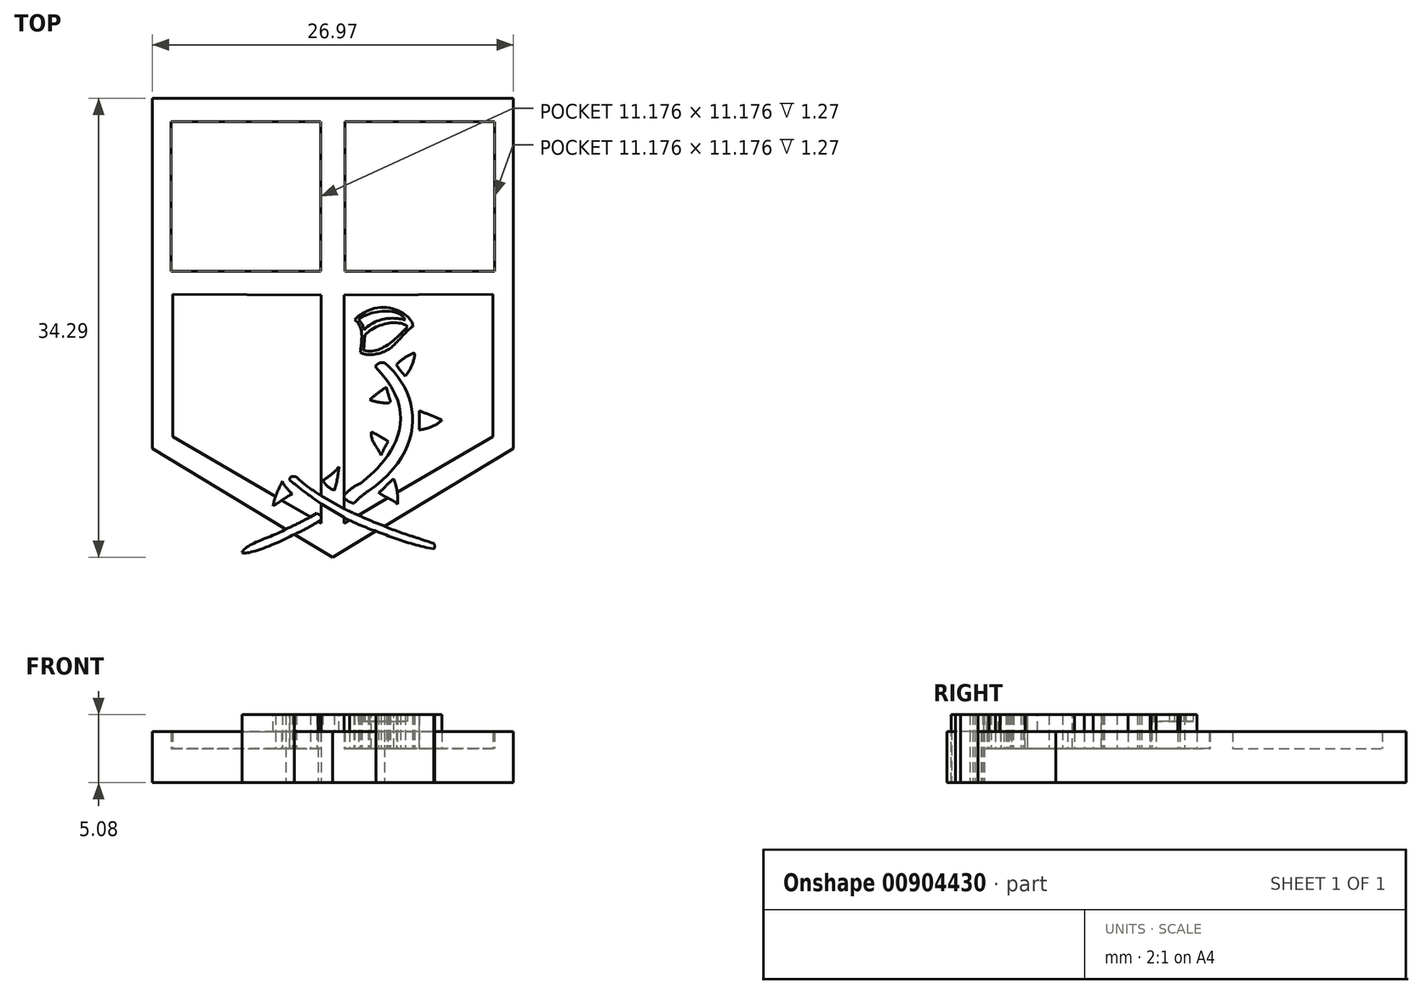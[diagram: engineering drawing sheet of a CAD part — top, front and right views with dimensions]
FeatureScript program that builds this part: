
annotation { "Feature Type Name" : "Feature", "Feature Type Description" : "" }
export const myFeature = defineFeature(function(context is Context, id is Id, definition is map)
    precondition{}
    {
        {
            var Q0;
            Q0=qCreatedBy(makeId("Top.planeOp"),FACE);
            var sketch = newSketch(context, id + "F0", { "sketchPlane" : qUnion([Q0])});
            skLineSegment(sketch, "E0", {"start": v(-8.88, 24.55) * mm, "end": v(18.1, 24.55) * mm});
            skLineSegment(sketch, "E1", {"start": v(18.1, 24.55) * mm, "end": v(18.1, -1.61) * mm});
            skLineSegment(sketch, "E2", {"start": v(-8.88, 24.55) * mm, "end": v(-8.88, -1.61) * mm});
            skPoint(sketch, "E3.endSnap0", {"position": v(4.6, -10.54) * mm});
            skLineSegment(sketch, "E4", {"start": v(-8.88, -1.61) * mm, "end": v(4.6, -9.74) * mm});
            skLineSegment(sketch, "E5", {"start": v(18.1, -1.61) * mm, "end": v(4.6, -9.74) * mm});
            skPoint(sketch, "E6", {"position": v(4.6, -9.27) * mm});
            skFitSpline(sketch, "E7", {"points": [v(1.75, -8.02) * mm, v(-2.16, -9.4) * mm], "startDerivative": vector(-3.65, -1.95) * mm, "endDerivative": vector(-1.46, 0.61) * mm});
            skFitSpline(sketch, "E8", {"points": [v(-2.16, -9.4) * mm, v(1.1, -7.64) * mm], "startDerivative": vector(0.54, 2) * mm, "endDerivative": vector(3.2, 1.91) * mm});
            skFitSpline(sketch, "E9", {"points": [v(12.16, -9.11) * mm, v(12.16, -8.7) * mm], "startDerivative": vector(0.36, 0.66) * mm, "endDerivative": vector(-0.03, 0.11) * mm});
            skLineSegment(sketch, "E10", {"start": v(-7.35, 9.92) * mm, "end": v(-7.35, -0.73) * mm});
            skLineSegment(sketch, "E11", {"start": v(-7.35, -0.73) * mm, "end": v(3.75, -7.2) * mm});
            skLineSegment(sketch, "E12", {"start": v(3.75, -7.2) * mm, "end": v(3.75, 9.86) * mm});
            skLineSegment(sketch, "E13", {"start": v(3.75, 9.86) * mm, "end": v(-7.35, 9.92) * mm});
            skLineSegment(sketch, "E14.MirrorCS", {"start": v(5.46, -7.2) * mm, "end": v(5.46, 9.86) * mm});
            skLineSegment(sketch, "E15.MirrorCS", {"start": v(5.46, 9.86) * mm, "end": v(16.56, 9.92) * mm});
            skLineSegment(sketch, "E16.MirrorCS", {"start": v(16.56, 9.92) * mm, "end": v(16.56, -0.73) * mm});
            skLineSegment(sketch, "E17.MirrorCS", {"start": v(16.56, -0.73) * mm, "end": v(5.46, -7.2) * mm});
            skLineSegment(sketch, "E18", {"start": v(-7.48, 11.6) * mm, "end": v(3.7, 11.6) * mm});
            skLineSegment(sketch, "E19", {"start": v(3.7, 11.6) * mm, "end": v(3.7, 22.79) * mm});
            skLineSegment(sketch, "E20", {"start": v(3.7, 22.79) * mm, "end": v(-7.48, 22.79) * mm});
            skLineSegment(sketch, "E21", {"start": v(-7.48, 22.79) * mm, "end": v(-7.48, 11.6) * mm});
            skLineSegment(sketch, "E22.MirrorCS", {"start": v(5.51, 11.6) * mm, "end": v(5.51, 22.79) * mm});
            skLineSegment(sketch, "E23.MirrorCS", {"start": v(5.51, 22.79) * mm, "end": v(16.69, 22.79) * mm});
            skLineSegment(sketch, "E24.MirrorCS", {"start": v(16.69, 11.6) * mm, "end": v(5.51, 11.6) * mm});
            skLineSegment(sketch, "E25.MirrorCS", {"start": v(16.69, 22.79) * mm, "end": v(16.69, 11.6) * mm});
            skFitSpline(sketch, "E26", {"points": [v(7.84, -7.79) * mm, v(12.16, -9.11) * mm], "startDerivative": vector(4.26, -1.68) * mm, "endDerivative": vector(4.49, -0.76) * mm});
            skFitSpline(sketch, "E27", {"points": [v(8.47, -7.41) * mm, v(12.16, -8.7) * mm], "startDerivative": vector(3.35, -1.51) * mm, "endDerivative": vector(3.74, -1.29) * mm});
            skFitSpline(sketch, "E28", {"points": [v(8.47, -7.41) * mm, v(6.52, -6.59) * mm], "startDerivative": vector(-2.19, 0.84) * mm, "endDerivative": vector(-1.81, 0.92) * mm});
            skFitSpline(sketch, "E29", {"points": [v(5.86, -6.98) * mm, v(7.84, -7.79) * mm], "startDerivative": vector(1.98, -1) * mm, "endDerivative": vector(2.05, -0.7) * mm});
            skFitSpline(sketch, "E30", {"points": [v(5.86, -6.98) * mm, v(5.46, -6.77) * mm], "startDerivative": vector(-0.5, 0.16) * mm, "endDerivative": vector(-0.31, 0.24) * mm});
            skLineSegment(sketch, "E31", {"start": v(5.46, -6.77) * mm, "end": v(3.75, -5.74) * mm});
            skFitSpline(sketch, "E32", {"points": [v(1.4, -3.97) * mm, v(1.89, -3.75) * mm], "startDerivative": vector(-0.2, 1.1) * mm, "endDerivative": vector(0.2, -0.15) * mm});
            skFitSpline(sketch, "E33", {"points": [v(3.75, -5.74) * mm, v(1.4, -3.97) * mm], "startDerivative": vector(-2.5, 1.72) * mm, "endDerivative": vector(-2.23, 1.88) * mm});
            skFitSpline(sketch, "E34", {"points": [v(1.89, -3.75) * mm, v(3.75, -5.14) * mm], "startDerivative": vector(1.45, -1.45) * mm, "endDerivative": vector(2.03, -1.25) * mm});
            skLineSegment(sketch, "E35", {"start": v(3.75, -5.14) * mm, "end": v(5.46, -6.11) * mm});
            skFitSpline(sketch, "E36", {"points": [v(5.46, -6.11) * mm, v(6.52, -6.59) * mm], "startDerivative": vector(0.85, -0.41) * mm, "endDerivative": vector(1.1, -0.4) * mm});
            skFitSpline(sketch, "E37", {"points": [v(1.75, -8.02) * mm, v(3.52, -7.07) * mm], "startDerivative": vector(1.94, 0.84) * mm, "endDerivative": vector(1.5, 1.02) * mm});
            skFitSpline(sketch, "E38", {"points": [v(2.94, -6.74) * mm, v(1.1, -7.64) * mm], "startDerivative": vector(-1.7, -0.83) * mm, "endDerivative": vector(-1.92, -0.81) * mm});
            skLineSegment(sketch, "E39", {"start": v(2.94, -6.74) * mm, "end": v(3.42, -6.45) * mm});
            skLineSegment(sketch, "E40", {"start": v(3.42, -6.45) * mm, "end": v(3.95, -6.8) * mm});
            skLineSegment(sketch, "E41", {"start": v(3.95, -6.8) * mm, "end": v(3.52, -7.07) * mm});
            skFitSpline(sketch, "E42", {"points": [v(8.03, -4.9) * mm, v(9.45, -5.78) * mm], "startDerivative": vector(1.28, -1) * mm, "endDerivative": vector(1.12, -1.08) * mm});
            skFitSpline(sketch, "E43", {"points": [v(9.45, -5.78) * mm, v(9.15, -3.88) * mm], "startDerivative": vector(0.12, 1.99) * mm, "endDerivative": vector(-0.76, 1.93) * mm});
            skFitSpline(sketch, "E44", {"points": [v(9.15, -3.88) * mm, v(8.03, -4.9) * mm], "startDerivative": vector(-1.28, -0.9) * mm, "endDerivative": vector(-0.9, -0.5) * mm});
            skFitSpline(sketch, "E45", {"points": [v(3.87, -4) * mm, v(5.07, -2.97) * mm], "startDerivative": vector(1.37, 0.85) * mm, "endDerivative": vector(1.04, 1.3) * mm});
            skFitSpline(sketch, "E46", {"points": [v(5.07, -2.97) * mm, v(4.73, -4.75) * mm], "startDerivative": vector(-0.15, -1.83) * mm, "endDerivative": vector(-0.54, -1.7) * mm});
            skFitSpline(sketch, "E47", {"points": [v(4.73, -4.75) * mm, v(3.87, -4) * mm], "startDerivative": vector(-1.15, 0.48) * mm, "endDerivative": vector(-0.35, 0.92) * mm});
            skFitSpline(sketch, "E48", {"points": [v(0.16, -5.9) * mm, v(0.85, -4.05) * mm], "startDerivative": vector(0.2, 1.87) * mm, "endDerivative": vector(0.89, 1.88) * mm});
            skFitSpline(sketch, "E49", {"points": [v(1.57, -5.02) * mm, v(0.85, -4.05) * mm], "startDerivative": vector(-0.88, 0.94) * mm, "endDerivative": vector(-0.18, 0.91) * mm});
            skFitSpline(sketch, "E50", {"points": [v(1.57, -5.02) * mm, v(0.16, -5.9) * mm], "startDerivative": vector(-1.49, -0.74) * mm, "endDerivative": vector(-1.1, -0.6) * mm});
            skFitSpline(sketch, "E51", {"points": [v(7.78, 4.5) * mm, v(6.68, -4.2) * mm], "startDerivative": vector(11.95, -11.98) * mm, "endDerivative": vector(-5.34, -3.98) * mm});
            skFitSpline(sketch, "E52", {"points": [v(7.25, -4.8) * mm, v(8.45, 4.81) * mm], "startDerivative": vector(12.9, 8.87) * mm, "endDerivative": vector(-8.74, 7.47) * mm});
            skFitSpline(sketch, "E53", {"points": [v(8.45, 4.81) * mm, v(7.78, 4.5) * mm], "startDerivative": vector(-0.97, 0.03) * mm, "endDerivative": vector(-0.4, -0.7) * mm});
            skFitSpline(sketch, "E54", {"points": [v(6.19, -5.71) * mm, v(5.34, -5.22) * mm], "startDerivative": vector(-0.98, 0.12) * mm, "endDerivative": vector(-0.63, 0.58) * mm});
            skFitSpline(sketch, "E55", {"points": [v(6.68, -4.2) * mm, v(5.34, -5.22) * mm], "startDerivative": vector(-1.96, -0.9) * mm, "endDerivative": vector(-1.14, -1.14) * mm});
            skFitSpline(sketch, "E56", {"points": [v(7.25, -4.8) * mm, v(6.19, -5.71) * mm], "startDerivative": vector(-1.17, -0.88) * mm, "endDerivative": vector(-1, -1.1) * mm});
            skFitSpline(sketch, "E57", {"points": [v(11.09, 1.2) * mm, v(12.76, 0.5) * mm], "startDerivative": vector(1.54, -0.64) * mm, "endDerivative": vector(1.6, -0.83) * mm});
            skFitSpline(sketch, "E58", {"points": [v(12.76, 0.5) * mm, v(11.06, -0.22) * mm], "startDerivative": vector(-1.18, -1.1) * mm, "endDerivative": vector(-2.39, -0.32) * mm});
            skFitSpline(sketch, "E59", {"points": [v(11.06, -0.22) * mm, v(11.09, 1.2) * mm], "startDerivative": vector(0.15, 1.56) * mm, "endDerivative": vector(0.02, 1.29) * mm});
            skFitSpline(sketch, "E60", {"points": [v(8.61, 2.97) * mm, v(8.92, 1.9) * mm], "startDerivative": vector(0.27, -1.1) * mm, "endDerivative": vector(0.42, -1.11) * mm});
            skFitSpline(sketch, "E61", {"points": [v(8.92, 1.9) * mm, v(8.8, 1.78) * mm], "startDerivative": vector(-0.17, -0.04) * mm, "endDerivative": vector(-0.09, -0.2) * mm});
            skFitSpline(sketch, "E62", {"points": [v(8.8, 1.78) * mm, v(7.36, 2.02) * mm], "startDerivative": vector(-1.48, -0.03) * mm, "endDerivative": vector(-1.23, 0.43) * mm});
            skFitSpline(sketch, "E63", {"points": [v(7.36, 2.02) * mm, v(8.61, 2.97) * mm], "startDerivative": vector(1.2, 1.04) * mm, "endDerivative": vector(1.34, 0.77) * mm});
            skFitSpline(sketch, "E64", {"points": [v(9.37, 4.66) * mm, v(10.02, 3.79) * mm], "startDerivative": vector(0.47, -0.95) * mm, "endDerivative": vector(0.76, -0.8) * mm});
            skFitSpline(sketch, "E65", {"points": [v(10.02, 3.79) * mm, v(10.73, 5.44) * mm], "startDerivative": vector(1.13, 1.35) * mm, "endDerivative": vector(0.16, 1.94) * mm});
            skFitSpline(sketch, "E66", {"points": [v(10.73, 5.44) * mm, v(10.65, 5.52) * mm], "startDerivative": vector(-0.05, 0.12) * mm, "endDerivative": vector(-0.1, 0) * mm});
            skFitSpline(sketch, "E67", {"points": [v(10.65, 5.52) * mm, v(9.37, 4.66) * mm], "startDerivative": vector(-1.45, -0.6) * mm, "endDerivative": vector(-1.01, -1.07) * mm});
            skFitSpline(sketch, "E68", {"points": [v(7.5, -0.37) * mm, v(8.76, -1.1) * mm], "startDerivative": vector(1.25, -0.62) * mm, "endDerivative": vector(1.27, -0.81) * mm});
            skFitSpline(sketch, "E69", {"points": [v(8.76, -1.1) * mm, v(8.22, -2.12) * mm], "startDerivative": vector(-0.7, -0.88) * mm, "endDerivative": vector(-0.4, -1.1) * mm});
            skFitSpline(sketch, "E70", {"points": [v(8.22, -2.12) * mm, v(7.5, -0.37) * mm], "startDerivative": vector(-0.73, 1.75) * mm, "endDerivative": vector(0.36, 2.07) * mm});
            skFitSpline(sketch, "E71", {"points": [v(6.53, 7.97) * mm, v(10.03, 8) * mm], "startDerivative": vector(1.06, 1.69) * mm, "endDerivative": vector(1.74, -3.54) * mm});
            skFitSpline(sketch, "E72", {"points": [v(10.03, 8) * mm, v(6.95, 7.24) * mm], "startDerivative": vector(-2.3, 0.65) * mm, "endDerivative": vector(-2.9, -3.02) * mm});
            skFitSpline(sketch, "E73", {"points": [v(6.92, 5.73) * mm, v(10.19, 7.48) * mm], "startDerivative": vector(3.52, -1.1) * mm, "endDerivative": vector(2.85, 3.03) * mm});
            skFitSpline(sketch, "E74", {"points": [v(10.19, 7.48) * mm, v(7.02, 6.87) * mm], "startDerivative": vector(-1.75, 1.7) * mm, "endDerivative": vector(-2.5, -2.76) * mm});
            skFitSpline(sketch, "E75", {"points": [v(6.53, 7.97) * mm, v(6.95, 7.24) * mm], "startDerivative": vector(0.64, -0.49) * mm, "endDerivative": vector(0.13, -1) * mm});
            skFitSpline(sketch, "E76", {"points": [v(7.02, 6.87) * mm, v(6.92, 5.73) * mm], "startDerivative": vector(-0.1, -1.14) * mm, "endDerivative": vector(-0.1, -1.14) * mm});
            skFitSpline(sketch, "E77", {"points": [v(6.24, 8) * mm, v(6.66, 5.57) * mm], "startDerivative": vector(2.32, -1.68) * mm, "endDerivative": vector(-0.2, -2.32) * mm});
            skFitSpline(sketch, "E78", {"points": [v(6.66, 5.57) * mm, v(8.91, 5.87) * mm], "startDerivative": vector(0.96, -0.74) * mm, "endDerivative": vector(2.53, 1.73) * mm});
            skFitSpline(sketch, "E79", {"points": [v(8.91, 5.87) * mm, v(10.59, 7.5) * mm], "startDerivative": vector(1.91, 1.72) * mm, "endDerivative": vector(1.75, 1.27) * mm});
            skFitSpline(sketch, "E80", {"points": [v(10.59, 7.5) * mm, v(10.57, 7.67) * mm], "startDerivative": vector(-0.02, 0.16) * mm, "endDerivative": vector(-0.02, 0.16) * mm});
            skFitSpline(sketch, "E81", {"points": [v(10.57, 7.67) * mm, v(6.24, 8) * mm], "startDerivative": vector(-0.95, 2.95) * mm, "endDerivative": vector(-5.37, -5.32) * mm});
            skSolve(sketch);
        }
        {
            var Q0;
            {var subQ5=sQuery(id+"F0.wireOp",EDGE,"E29");Q0=makeQuery(id+"F0.imprint","IMPRINT",FACE,{"disambiguationData":[TD([[makeQuery(id+"F0.imprint","IMPRINT",EDGE,{"derivedFrom":subQ5}),-1.0]])]});}
            var Q1;
            {var subQ0=sQuery(id+"F0.wireOp",EDGE,"E41");var subQ1=sQuery(id+"F0.wireOp",EDGE,"E12");var subQ2=makeQuery(id+"F0.imprint","INTERSECT",VERTEX,{"derivedFrom":[subQ1,subQ0]});Q1=makeQuery(id+"F0.imprint","IMPRINT",FACE,{"disambiguationData":[TD([[makeQuery(id+"F0.imprint","IMPRINT",EDGE,{"disambiguationData":[TD([[subQ2,-1.0]])],"derivedFrom":subQ1}),-1.0]])]});}
            var Q2;
            Q2=makeQuery(id+"F0.imprint","IMPRINT",FACE,{"disambiguationData":[TD([[makeQuery(id+"F0.imprint","IMPRINT",EDGE,{"derivedFrom":sQuery(id+"F0.wireOp",EDGE,"E0")}),-1.0]])]});
            var Q3;
            {var subQ0=sQuery(id+"F0.wireOp",EDGE,"E54");var subQ1=sQuery(id+"F0.wireOp",EDGE,"E14.MirrorCS");var subQ2=makeQuery(id+"F0.imprint","INTERSECT",VERTEX,{"derivedFrom":[subQ1,subQ0]});Q3=makeQuery(id+"F0.imprint","IMPRINT",FACE,{"disambiguationData":[TD([[makeQuery(id+"F0.imprint","IMPRINT",EDGE,{"disambiguationData":[TD([[subQ2,-1.0]])],"derivedFrom":subQ1}),1.0]])]});}
            extrude(context, id + "F1", {"entities" : qUnion([Q0, Q1, Q2, Q3]), "depth" : 3.8 * mm, "offsetDistance" : 25.4 * mm});
        }
        {
            var Q0;
            Q0=makeQuery(id+"F0.imprint","IMPRINT",FACE,{"disambiguationData":[TD([[makeQuery(id+"F0.imprint","IMPRINT",EDGE,{"derivedFrom":sQuery(id+"F0.wireOp",EDGE,"E18")}),1.0]])]});
            var Q1;
            Q1=makeQuery(id+"F0.imprint","IMPRINT",FACE,{"disambiguationData":[TD([[makeQuery(id+"F0.imprint","IMPRINT",EDGE,{"derivedFrom":sQuery(id+"F0.wireOp",EDGE,"E22.MirrorCS")}),-1.0]])]});
            var Q2;
            Q2=makeQuery(id+"F0.imprint","IMPRINT",FACE,{"disambiguationData":[TD([[makeQuery(id+"F0.imprint","IMPRINT",EDGE,{"derivedFrom":sQuery(id+"F0.wireOp",EDGE,"E14.MirrorCS")}),-1.0]])]});
            var Q3;
            Q3=makeQuery(id+"F0.imprint","IMPRINT",FACE,{"disambiguationData":[TD([[makeQuery(id+"F0.imprint","IMPRINT",EDGE,{"derivedFrom":sQuery(id+"F0.wireOp",EDGE,"E10")}),1.0]])]});
            var Q4;
            {var subQ4=sQuery(id+"F0.wireOp",EDGE,"E15.MirrorCS");Q4=makeQuery(id+"F0.imprint","IMPRINT",FACE,{"disambiguationData":[TD([[makeQuery(id+"F0.imprint","IMPRINT",EDGE,{"derivedFrom":subQ4}),-1.0]])]});}
            extrude(context, id + "F2", {"entities" : qUnion([Q0, Q1, Q2, Q3, Q4]), "operationType" : NewBodyOperationType.ADD, "depth" : 2.54 * mm, "offsetDistance" : 25.4 * mm});
        }
        {
            var Q0;
            {var subQ5=sQuery(id+"F0.wireOp",EDGE,"E49");Q0=makeQuery(id+"F0.imprint","IMPRINT",FACE,{"disambiguationData":[TD([[makeQuery(id+"F0.imprint","IMPRINT",EDGE,{"derivedFrom":subQ5}),1.0]])]});}
            var Q1;
            {var subQ0=sQuery(id+"F0.wireOp",EDGE,"E48");var subQ1=sQuery(id+"F0.wireOp",EDGE,"E11");var subQ2=makeQuery(id+"F0.imprint","INTERSECT",VERTEX,{"derivedFrom":[subQ1,subQ0]});Q1=makeQuery(id+"F0.imprint","IMPRINT",FACE,{"disambiguationData":[TD([[makeQuery(id+"F0.imprint","IMPRINT",EDGE,{"disambiguationData":[TD([[subQ2,-1.0]])],"derivedFrom":subQ1}),-1.0]])]});}
            var Q2;
            {var subQ0=sQuery(id+"F0.wireOp",EDGE,"E7");Q2=makeQuery(id+"F0.imprint","IMPRINT",FACE,{"disambiguationData":[TD([[makeQuery(id+"F0.imprint","IMPRINT",EDGE,{"derivedFrom":subQ0}),-1.0]])]});}
            var Q3;
            {var subQ0=sQuery(id+"F0.wireOp",EDGE,"E37");Q3=makeQuery(id+"F0.imprint","IMPRINT",FACE,{"disambiguationData":[TD([[makeQuery(id+"F0.imprint","IMPRINT",EDGE,{"derivedFrom":subQ0}),1.0]])]});}
            var Q4;
            {var subQ1=sQuery(id+"F0.wireOp",EDGE,"E39");Q4=makeQuery(id+"F0.imprint","IMPRINT",FACE,{"disambiguationData":[TD([[makeQuery(id+"F0.imprint","IMPRINT",EDGE,{"derivedFrom":subQ1}),-1.0]])]});}
            var Q5;
            {var subQ0=sQuery(id+"F0.wireOp",EDGE,"E31");Q5=makeQuery(id+"F0.imprint","IMPRINT",FACE,{"disambiguationData":[TD([[makeQuery(id+"F0.imprint","IMPRINT",EDGE,{"derivedFrom":subQ0}),-1.0]])]});}
            var Q6;
            Q6=makeQuery(id+"F0.imprint","IMPRINT",FACE,{"disambiguationData":[TD([[makeQuery(id+"F0.imprint","IMPRINT",EDGE,{"derivedFrom":sQuery(id+"F0.wireOp",EDGE,"E32")}),-1.0]])]});
            var Q7;
            {var subQ0=sQuery(id+"F0.wireOp",EDGE,"E30");Q7=makeQuery(id+"F0.imprint","IMPRINT",FACE,{"disambiguationData":[TD([[makeQuery(id+"F0.imprint","IMPRINT",EDGE,{"derivedFrom":subQ0}),-1.0]])]});}
            var Q8;
            Q8=makeQuery(id+"F0.imprint","IMPRINT",FACE,{"disambiguationData":[TD([[makeQuery(id+"F0.imprint","IMPRINT",EDGE,{"derivedFrom":sQuery(id+"F0.wireOp",EDGE,"E9")}),1.0]])]});
            var Q9;
            {var subQ0=sQuery(id+"F0.wireOp",EDGE,"E51");Q9=makeQuery(id+"F0.imprint","IMPRINT",FACE,{"disambiguationData":[TD([[makeQuery(id+"F0.imprint","IMPRINT",EDGE,{"derivedFrom":subQ0}),1.0]])]});}
            var Q10;
            {var subQ5=sQuery(id+"F0.wireOp",EDGE,"E44");Q10=makeQuery(id+"F0.imprint","IMPRINT",FACE,{"disambiguationData":[TD([[makeQuery(id+"F0.imprint","IMPRINT",EDGE,{"derivedFrom":subQ5}),1.0]])]});}
            var Q11;
            {var subQ0=sQuery(id+"F0.wireOp",EDGE,"E43");var subQ1=sQuery(id+"F0.wireOp",EDGE,"E17.MirrorCS");var subQ2=makeQuery(id+"F0.imprint","INTERSECT",VERTEX,{"derivedFrom":[subQ1,subQ0]});Q11=makeQuery(id+"F0.imprint","IMPRINT",FACE,{"disambiguationData":[TD([[makeQuery(id+"F0.imprint","IMPRINT",EDGE,{"disambiguationData":[TD([[subQ2,-1.0]])],"derivedFrom":subQ1}),1.0]])]});}
            var Q12;
            Q12=makeQuery(id+"F0.imprint","IMPRINT",FACE,{"disambiguationData":[TD([[makeQuery(id+"F0.imprint","IMPRINT",EDGE,{"derivedFrom":sQuery(id+"F0.wireOp",EDGE,"E68")}),-1.0]])]});
            var Q13;
            Q13=makeQuery(id+"F0.imprint","IMPRINT",FACE,{"disambiguationData":[TD([[makeQuery(id+"F0.imprint","IMPRINT",EDGE,{"derivedFrom":sQuery(id+"F0.wireOp",EDGE,"E57")}),-1.0]])]});
            var Q14;
            Q14=makeQuery(id+"F0.imprint","IMPRINT",FACE,{"disambiguationData":[TD([[makeQuery(id+"F0.imprint","IMPRINT",EDGE,{"derivedFrom":sQuery(id+"F0.wireOp",EDGE,"E60")}),-1.0]])]});
            var Q15;
            Q15=makeQuery(id+"F0.imprint","IMPRINT",FACE,{"disambiguationData":[TD([[makeQuery(id+"F0.imprint","IMPRINT",EDGE,{"derivedFrom":sQuery(id+"F0.wireOp",EDGE,"E64")}),1.0]])]});
            var Q16;
            Q16=makeQuery(id+"F0.imprint","IMPRINT",FACE,{"disambiguationData":[TD([[makeQuery(id+"F0.imprint","IMPRINT",EDGE,{"derivedFrom":sQuery(id+"F0.wireOp",EDGE,"E45")}),-1.0]])]});
            var Q17;
            {var subQ2=sQuery(id+"F0.wireOp",EDGE,"E28");Q17=makeQuery(id+"F0.imprint","IMPRINT",FACE,{"disambiguationData":[TD([[makeQuery(id+"F0.imprint","IMPRINT",EDGE,{"derivedFrom":subQ2}),1.0]])]});}
            var Q18;
            Q18=makeQuery(id+"F0.imprint","IMPRINT",FACE,{"disambiguationData":[TD([[makeQuery(id+"F0.imprint","IMPRINT",EDGE,{"derivedFrom":sQuery(id+"F0.wireOp",EDGE,"E71")}),1.0]])]});
            extrude(context, id + "F3", {"entities" : qUnion([Q0, Q1, Q2, Q3, Q4, Q5, Q6, Q7, Q8, Q9, Q10, Q11, Q12, Q13, Q14, Q15, Q16, Q17, Q18]), "operationType" : NewBodyOperationType.ADD, "depth" : 5.08 * mm, "offsetDistance" : 25.4 * mm});
        }
        {
            var Q0;
            Q0=makeQuery(id+"F0.imprint","IMPRINT",FACE,{"disambiguationData":[TD([[makeQuery(id+"F0.imprint","IMPRINT",EDGE,{"derivedFrom":sQuery(id+"F0.wireOp",EDGE,"E73")}),1.0]])]});
            var Q1;
            Q1=makeQuery(id+"F0.imprint","IMPRINT",FACE,{"disambiguationData":[TD([[makeQuery(id+"F0.imprint","IMPRINT",EDGE,{"derivedFrom":sQuery(id+"F0.wireOp",EDGE,"E71")}),-1.0]])]});
            extrude(context, id + "F4", {"entities" : qUnion([Q0, Q1]), "operationType" : NewBodyOperationType.ADD, "depth" : 4.57 * mm, "offsetDistance" : 25.4 * mm});
        }
    });
